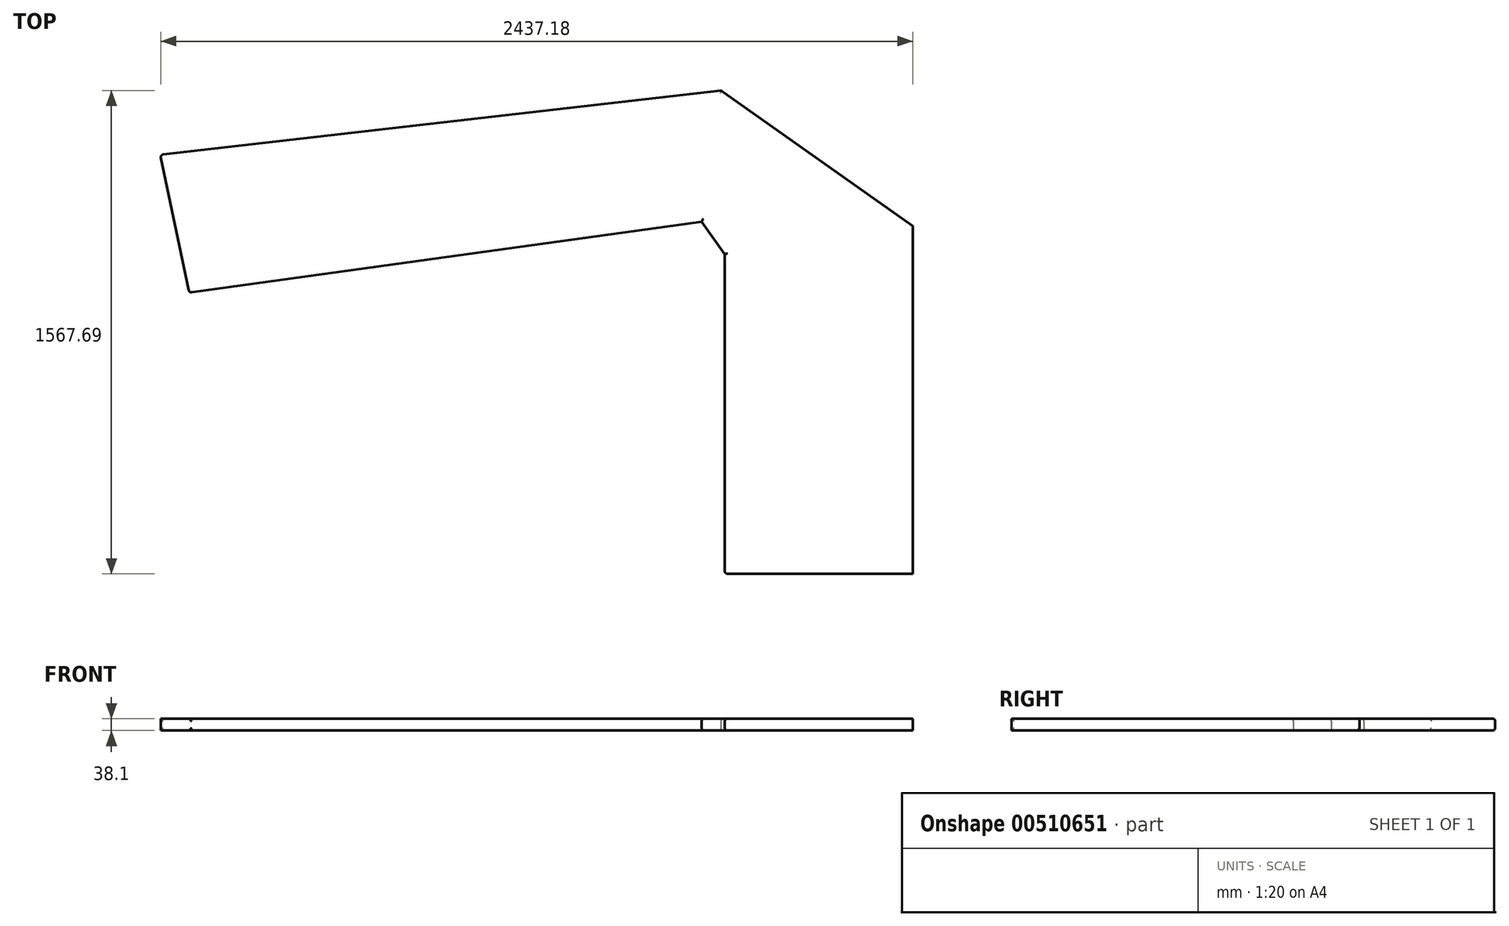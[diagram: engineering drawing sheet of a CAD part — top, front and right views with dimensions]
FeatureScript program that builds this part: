
annotation { "Feature Type Name" : "Feature", "Feature Type Description" : "" }
export const myFeature = defineFeature(function(context is Context, id is Id, definition is map)
    precondition{}
    {
        {
            var Q0;
            Q0=qCreatedBy(makeId("Top.planeOp"),FACE);
            var sketch = newSketch(context, id + "F0", { "sketchPlane" : qUnion([Q0])});
            skLineSegment(sketch, "E0", {"start": v(-1378.24, 502.83) * mm, "end": v(282.36, 732.4) * mm});
            skLineSegment(sketch, "E1", {"start": v(282.36, 732.4) * mm, "end": v(357.02, 627.46) * mm});
            skLineSegment(sketch, "E2", {"start": v(357.02, 627.46) * mm, "end": v(357.02, -408.86) * mm});
            skLineSegment(sketch, "E3", {"start": v(357.02, -408.86) * mm, "end": v(966.62, -408.86) * mm});
            skLineSegment(sketch, "E4", {"start": v(966.62, -408.86) * mm, "end": v(966.62, 718.9) * mm});
            skLineSegment(sketch, "E5", {"start": v(966.62, 718.9) * mm, "end": v(344.43, 1158.83) * mm});
            skLineSegment(sketch, "E6", {"start": v(344.43, 1158.83) * mm, "end": v(-1472.43, 950.22) * mm});
            skLineSegment(sketch, "E7", {"start": v(-1472.43, 950.22) * mm, "end": v(-1378.24, 502.83) * mm});
            skSolve(sketch);
        }
        {
            var Q0;
            Q0 = qSketchRegion(id + "F0", true);
            extrude(context, id + "F1", {"entities" : qUnion([Q0]), "depth" : 38.1 * mm, "offsetDistance" : 30.48 * mm});
        }
        {
            var Q0;
            Q0=makeQuery(id+"F1.opExtrude","CAP_EDGE",EDGE,{"disambiguationData":[OSD([sQuery(id+"F0.wireOp",EDGE,"E0")])],"isStart":false});
            var Q1;
            Q1=makeQuery(id+"F1.opExtrude","CAP_EDGE",EDGE,{"disambiguationData":[OSD([sQuery(id+"F0.wireOp",EDGE,"E0")])],"isStart":true});
            var Q2;
            Q2=makeQuery(id+"F1.opExtrude","SWEPT_EDGE",EDGE,{"disambiguationData":[OSD([sQuery(id+"F0.wireOp",EDGE,"E0"),sQuery(id+"F0.wireOp",EDGE,"E7")])]});
            var Q3;
            Q3=makeQuery(id+"F1.opExtrude","CAP_EDGE",EDGE,{"disambiguationData":[OSD([sQuery(id+"F0.wireOp",EDGE,"E1")])],"isStart":true});
            var Q4;
            Q4=makeQuery(id+"F1.opExtrude","CAP_EDGE",EDGE,{"disambiguationData":[OSD([sQuery(id+"F0.wireOp",EDGE,"E2")])],"isStart":true});
            var Q5;
            Q5=makeQuery(id+"F1.opExtrude","CAP_EDGE",EDGE,{"disambiguationData":[OSD([sQuery(id+"F0.wireOp",EDGE,"E2")])],"isStart":false});
            var Q6;
            Q6=makeQuery(id+"F1.opExtrude","CAP_EDGE",EDGE,{"disambiguationData":[OSD([sQuery(id+"F0.wireOp",EDGE,"E1")])],"isStart":false});
            var Q7;
            Q7=makeQuery(id+"F1.opExtrude","SWEPT_EDGE",EDGE,{"disambiguationData":[OSD([sQuery(id+"F0.wireOp",EDGE,"E2"),sQuery(id+"F0.wireOp",EDGE,"E3")])]});
            var Q8;
            Q8=makeQuery(id+"F1.opExtrude","SWEPT_EDGE",EDGE,{"disambiguationData":[OSD([sQuery(id+"F0.wireOp",EDGE,"E6"),sQuery(id+"F0.wireOp",EDGE,"E7")])]});
            var Q9;
            Q9=makeQuery(id+"F1.opExtrude","CAP_EDGE",EDGE,{"disambiguationData":[OSD([sQuery(id+"F0.wireOp",EDGE,"E6")])],"isStart":false});
            var Q10;
            Q10=makeQuery(id+"F1.opExtrude","CAP_EDGE",EDGE,{"disambiguationData":[OSD([sQuery(id+"F0.wireOp",EDGE,"E6")])],"isStart":true});
            var Q11;
            Q11=makeQuery(id+"F1.opExtrude","CAP_EDGE",EDGE,{"disambiguationData":[OSD([sQuery(id+"F0.wireOp",EDGE,"E5")])],"isStart":true});
            fillet(context, id + "F2", {"entities" : qUnion([Q0, Q1, Q2, Q3, Q4, Q5, Q6, Q7, Q8, Q9, Q10, Q11]), "radius" : 9.14 * mm, "tangentPropagation" : true, "allowEdgeOverflow" : false});
        }
    });
